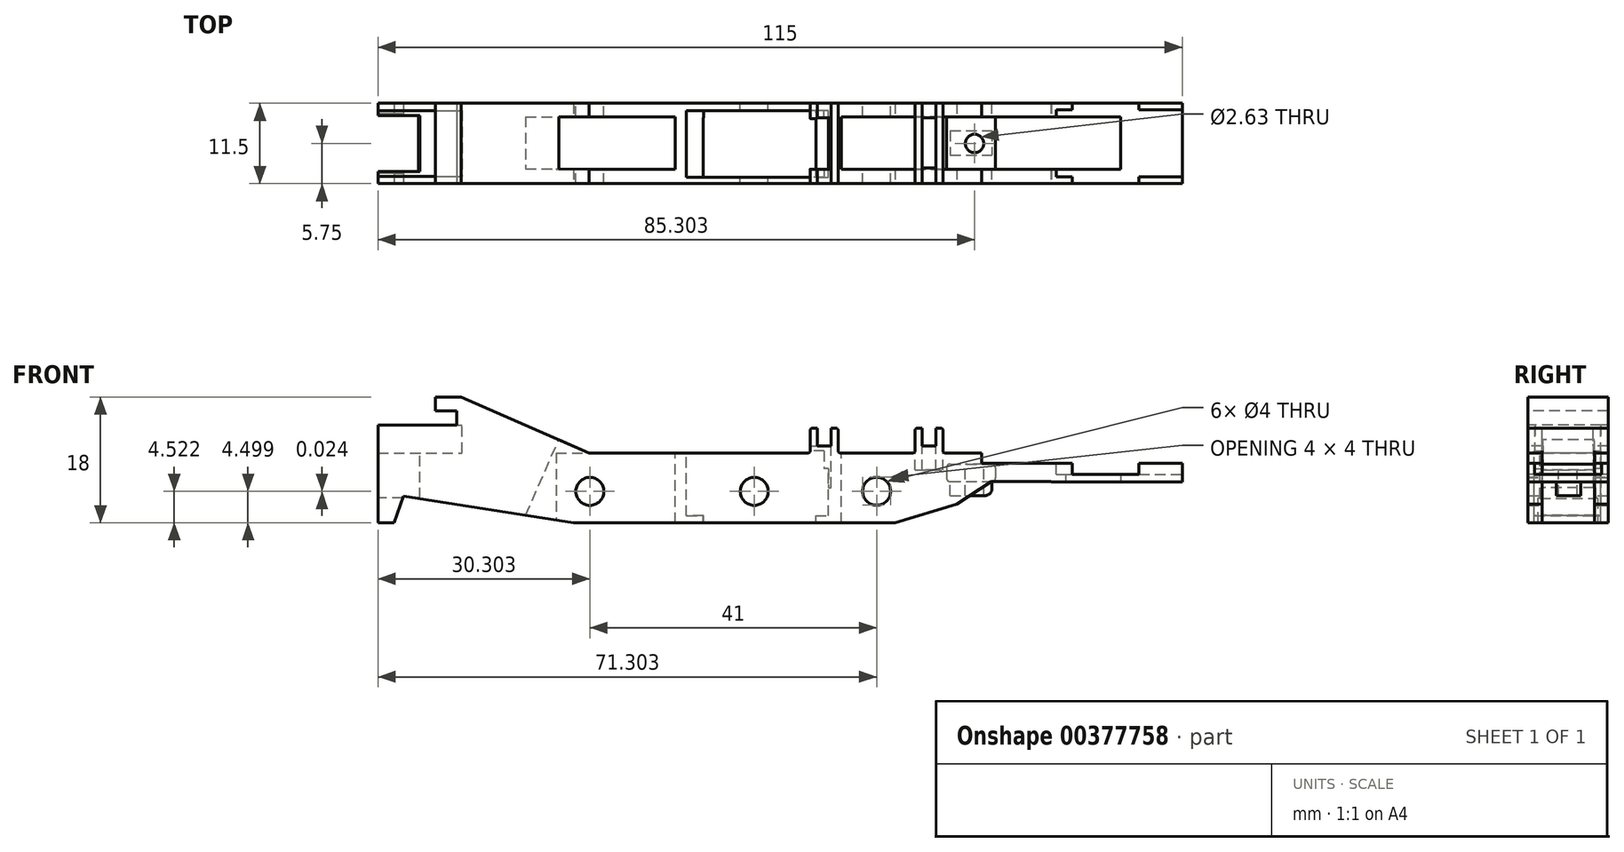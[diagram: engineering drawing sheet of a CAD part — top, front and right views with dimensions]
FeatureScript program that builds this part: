
annotation { "Feature Type Name" : "Feature", "Feature Type Description" : "" }
export const myFeature = defineFeature(function(context is Context, id is Id, definition is map)
    precondition{}
    {
        {
            var Q0;
            Q0=qCreatedBy(makeId("Front.planeOp"),FACE);
            var sketch = newSketch(context, id + "F0", { "sketchPlane" : qUnion([Q0])});
            skLineSegment(sketch, "E0.bottom", {"start": v(-37, -2.67) * mm, "end": v(77, -2.67) * mm});
            skLineSegment(sketch, "E0.top", {"start": v(-37, 7.33) * mm, "end": v(77, 7.33) * mm});
            skLineSegment(sketch, "E0.left", {"start": v(-37, -2.67) * mm, "end": v(-37, 7.33) * mm});
            skLineSegment(sketch, "E0.right", {"start": v(77, -2.67) * mm, "end": v(77, 7.33) * mm});
            skCircle(sketch, "E1", {"center": v(-7.7, 1.83) * mm, "radius": 2 * mm});
            skCircle(sketch, "E2", {"center": v(33.3, 1.85) * mm, "radius": 2 * mm});
            skCircle(sketch, "E3", {"center": v(15.8, 1.83) * mm, "radius": 2 * mm});
            skSolve(sketch);
        }
        {
            var Q0;
            Q0=makeQuery(id+"F0.imprint","IMPRINT",FACE,{"disambiguationData":[TD([[makeQuery(id+"F0.imprint","IMPRINT",EDGE,{"derivedFrom":sQuery(id+"F0.wireOp",EDGE,"E0.bottom")}),1.0]])]});
            extrude(context, id + "F1", {"entities" : qUnion([Q0]), "endBound" : BoundingType.SYMMETRIC, "depth" : 11.5 * mm});
        }
        {
            var Q0;
            Q0=makeQuery(id+"F1.opExtrude","SWEPT_FACE",FACE,{"disambiguationData":[OSD([sQuery(id+"F0.wireOp",EDGE,"E0.top")])]});
            var sketch = newSketch(context, id + "F2", { "sketchPlane" : qUnion([Q0])});
            skLineSegment(sketch, "E4.bottom", {"start": v(-33.33, 3.81) * mm, "end": v(4.47, 3.81) * mm});
            skLineSegment(sketch, "E4.top", {"start": v(-33.33, -3.69) * mm, "end": v(4.47, -3.69) * mm});
            skLineSegment(sketch, "E4.left", {"start": v(-33.33, 3.81) * mm, "end": v(-33.33, -3.69) * mm});
            skLineSegment(sketch, "E4.right", {"start": v(4.47, 3.81) * mm, "end": v(4.47, -3.69) * mm});
            skLineSegment(sketch, "E5.bottom", {"start": v(38.75, 3.81) * mm, "end": v(73.03, 3.81) * mm});
            skLineSegment(sketch, "E5.top", {"start": v(38.75, -3.69) * mm, "end": v(73.03, -3.69) * mm});
            skLineSegment(sketch, "E5.left", {"start": v(38.75, 3.81) * mm, "end": v(38.75, -3.69) * mm});
            skLineSegment(sketch, "E5.right", {"start": v(73.03, 3.81) * mm, "end": v(73.03, -3.69) * mm});
            skSolve(sketch);
        }
        {
            var Q0;
            Q0=makeQuery(id+"F2.imprint","IMPRINT",FACE,{"disambiguationData":[TD([[makeQuery(id+"F2.imprint","IMPRINT",EDGE,{"derivedFrom":sQuery(id+"F2.wireOp",EDGE,"E4.bottom")}),-1.0]])]});
            var Q1;
            Q1=makeQuery(id+"F2.imprint","IMPRINT",FACE,{"disambiguationData":[TD([[makeQuery(id+"F2.imprint","IMPRINT",EDGE,{"derivedFrom":sQuery(id+"F2.wireOp",EDGE,"E5.bottom")}),-1.0]])]});
            extrude(context, id + "F3", {"entities" : qUnion([Q0, Q1]), "operationType" : NewBodyOperationType.REMOVE, "endBound" : BoundingType.THROUGH_ALL, "oppositeDirection" : true, "depth" : 25 * mm});
        }
        {
            var Q0;
            Q0=makeQuery(id+"F1.opExtrude","SWEPT_FACE",FACE,{"disambiguationData":[OSD([sQuery(id+"F0.wireOp",EDGE,"E0.top")])]});
            var sketch = newSketch(context, id + "F4", { "sketchPlane" : qUnion([Q0])});
            skLineSegment(sketch, "E6.bottom", {"start": v(38.75, 3.81) * mm, "end": v(28.24, 3.81) * mm});
            skLineSegment(sketch, "E6.top", {"start": v(38.75, -3.69) * mm, "end": v(28.24, -3.69) * mm});
            skLineSegment(sketch, "E6.left", {"start": v(38.75, 3.81) * mm, "end": v(38.75, -3.69) * mm});
            skLineSegment(sketch, "E6.right", {"start": v(28.24, 3.81) * mm, "end": v(28.24, -3.69) * mm});
            skSolve(sketch);
        }
        {
            var Q0;
            Q0=makeQuery(id+"F4.imprint","IMPRINT",FACE,{"disambiguationData":[TD([[makeQuery(id+"F4.imprint","IMPRINT",EDGE,{"derivedFrom":sQuery(id+"F4.wireOp",EDGE,"E6.bottom")}),1.0]])]});
            extrude(context, id + "F5", {"entities" : qUnion([Q0]), "operationType" : NewBodyOperationType.REMOVE, "endBound" : BoundingType.THROUGH_ALL, "oppositeDirection" : true, "depth" : 25 * mm});
        }
        {
            var Q0;
            Q0=makeQuery(id+"F1.opExtrude","SWEPT_FACE",FACE,{"disambiguationData":[OSD([sQuery(id+"F0.wireOp",EDGE,"E0.top")])]});
            var sketch = newSketch(context, id + "F6", { "sketchPlane" : qUnion([Q0])});
            skLineSegment(sketch, "E7", {"start": v(6.12, 4.69) * mm, "end": v(6.12, -4.81) * mm});
            skLineSegment(sketch, "E8", {"start": v(6.12, -4.81) * mm, "end": v(26.4, -4.81) * mm});
            skLineSegment(sketch, "E9", {"start": v(26.4, -4.81) * mm, "end": v(26.4, 4.69) * mm});
            skLineSegment(sketch, "E10", {"start": v(26.4, 4.69) * mm, "end": v(6.12, 4.69) * mm});
            skSolve(sketch);
        }
        {
            var Q0;
            Q0=makeQuery(id+"F6.imprint","IMPRINT",FACE,{"disambiguationData":[TD([[makeQuery(id+"F6.imprint","IMPRINT",EDGE,{"derivedFrom":sQuery(id+"F6.wireOp",EDGE,"E7")}),1.0]])]});
            extrude(context, id + "F7", {"entities" : qUnion([Q0]), "operationType" : NewBodyOperationType.REMOVE, "endBound" : BoundingType.THROUGH_ALL, "oppositeDirection" : true, "depth" : 25 * mm});
        }
        {
            var Q0;
            Q0=makeQuery(id+"F1.opExtrude","CAP_FACE",FACE,{"disambiguationData":[OSD([sQuery(id+"F0.wireOp",EDGE,"E0.bottom"),sQuery(id+"F0.wireOp",EDGE,"E0.top"),sQuery(id+"F0.wireOp",EDGE,"E0.left"),sQuery(id+"F0.wireOp",EDGE,"E0.right"),sQuery(id+"F0.wireOp",EDGE,"E1"),sQuery(id+"F0.wireOp",EDGE,"saFeJPni-Uy6Z-6q54-hsxs-ZEZ7Dlqlj6Tq"),sQuery(id+"F0.wireOp",EDGE,"E2")])],"isStart":false});
            var sketch = newSketch(context, id + "F8", { "sketchPlane" : qUnion([Q0])});
            skLineSegment(sketch, "E11.bottom", {"start": v(60.3, 7.33) * mm, "end": v(75.3, 7.33) * mm});
            skLineSegment(sketch, "E11.top", {"start": v(60.3, -2.67) * mm, "end": v(75.3, -2.67) * mm});
            skLineSegment(sketch, "E11.left", {"start": v(60.3, 7.33) * mm, "end": v(60.3, -2.67) * mm});
            skLineSegment(sketch, "E11.right", {"start": v(75.3, 7.33) * mm, "end": v(75.3, -2.67) * mm});
            skSolve(sketch);
        }
        {
            var Q0;
            Q0=makeQuery(id+"F8.imprint","IMPRINT",FACE,{"disambiguationData":[TD([[makeQuery(id+"F8.imprint","IMPRINT",EDGE,{"derivedFrom":sQuery(id+"F8.wireOp",EDGE,"E11.bottom")}),-1.0]])]});
            extrude(context, id + "F9", {"entities" : qUnion([Q0]), "operationType" : NewBodyOperationType.ADD, "oppositeDirection" : true, "depth" : 11.5 * mm});
        }
        {
            var Q0;
            Q0=makeQuery(id+"F9.boolean.opBoolean","MERGE",FACE,{"derivedFrom":[makeQuery(id+"F1.opExtrude","SWEPT_FACE",FACE,{"disambiguationData":[OSD([sQuery(id+"F0.wireOp",EDGE,"E0.top")])]}),makeQuery(id+"F9.opExtrude","SWEPT_FACE",FACE,{"disambiguationData":[OSD([sQuery(id+"F8.wireOp",EDGE,"E11.bottom")])]})]});
            var sketch = newSketch(context, id + "F10", { "sketchPlane" : qUnion([Q0])});
            skArc(sketch, "E12", {"start": v(65.32, 1) * mm, "mid": v(64.3, -0.01) * mm, "end": v(65.34, -1) * mm});
            skArc(sketch, "E13", {"start": v(66.8, -1) * mm, "mid": v(67.8, 0) * mm, "end": v(66.8, 1) * mm});
            skLineSegment(sketch, "E14", {"start": v(65.28, 1) * mm, "end": v(66.8, 1) * mm});
            skLineSegment(sketch, "E15", {"start": v(65.34, -1) * mm, "end": v(66.8, -1) * mm});
            skSolve(sketch);
        }
        {
            var Q0;
            {var subQ3=sQuery(id+"F10.wireOp",EDGE,"E12");Q0=makeQuery(id+"F10.imprint","IMPRINT",FACE,{"disambiguationData":[TD([[makeQuery(id+"F10.imprint","IMPRINT",EDGE,{"derivedFrom":subQ3}),1.0]])]});}
            extrude(context, id + "F11", {"entities" : qUnion([Q0]), "operationType" : NewBodyOperationType.REMOVE, "endBound" : BoundingType.THROUGH_ALL, "oppositeDirection" : true, "depth" : 25 * mm});
        }
        {
            var Q0;
            Q0=makeQuery(id+"F1.opExtrude","CAP_FACE",FACE,{"disambiguationData":[OSD([sQuery(id+"F0.wireOp",EDGE,"E0.bottom"),sQuery(id+"F0.wireOp",EDGE,"E0.top"),sQuery(id+"F0.wireOp",EDGE,"E0.left"),sQuery(id+"F0.wireOp",EDGE,"E0.right"),sQuery(id+"F0.wireOp",EDGE,"E1"),sQuery(id+"F0.wireOp",EDGE,"saFeJPni-Uy6Z-6q54-hsxs-ZEZ7Dlqlj6Tq"),sQuery(id+"F0.wireOp",EDGE,"E2")])],"isStart":false});
            var sketch = newSketch(context, id + "F12", { "sketchPlane" : qUnion([Q0])});
            skLineSegment(sketch, "E16.bottom", {"start": v(48.3, 7.33) * mm, "end": v(77, 7.33) * mm});
            skLineSegment(sketch, "E16.top", {"start": v(48.3, 5.83) * mm, "end": v(61.3, 5.83) * mm});
            skLineSegment(sketch, "E16.left", {"start": v(48.3, 7.33) * mm, "end": v(48.3, 5.83) * mm});
            skLineSegment(sketch, "E16.right", {"start": v(77, 7.33) * mm, "end": v(77, 5.83) * mm});
            skLineSegment(sketch, "E17.top", {"start": v(61.3, 4.23) * mm, "end": v(70.8, 4.23) * mm});
            skLineSegment(sketch, "E17.left", {"start": v(61.3, 5.83) * mm, "end": v(61.3, 4.23) * mm});
            skLineSegment(sketch, "E17.right", {"start": v(70.8, 5.83) * mm, "end": v(70.8, 4.23) * mm});
            skLineSegment(sketch, "E18.trimOffspring", {"start": v(70.8, 5.83) * mm, "end": v(77, 5.83) * mm});
            skSolve(sketch);
        }
        {
            var Q0;
            Q0=makeQuery(id+"F12.imprint","IMPRINT",FACE,{"disambiguationData":[TD([[makeQuery(id+"F12.imprint","IMPRINT",EDGE,{"derivedFrom":sQuery(id+"F12.wireOp",EDGE,"E16.bottom")}),-1.0]])]});
            extrude(context, id + "F13", {"entities" : qUnion([Q0]), "operationType" : NewBodyOperationType.REMOVE, "endBound" : BoundingType.THROUGH_ALL, "oppositeDirection" : true, "depth" : 25 * mm});
        }
        {
            var Q0;
            Q0=makeQuery(id+"F1.opExtrude","CAP_FACE",FACE,{"disambiguationData":[OSD([sQuery(id+"F0.wireOp",EDGE,"E0.bottom"),sQuery(id+"F0.wireOp",EDGE,"E0.top"),sQuery(id+"F0.wireOp",EDGE,"E0.left"),sQuery(id+"F0.wireOp",EDGE,"E0.right"),sQuery(id+"F0.wireOp",EDGE,"E1"),sQuery(id+"F0.wireOp",EDGE,"saFeJPni-Uy6Z-6q54-hsxs-ZEZ7Dlqlj6Tq"),sQuery(id+"F0.wireOp",EDGE,"E2")])],"isStart":false});
            var sketch = newSketch(context, id + "F14", { "sketchPlane" : qUnion([Q0])});
            skLineSegment(sketch, "E19.bottom", {"start": v(50, -2.67) * mm, "end": v(77, -2.67) * mm});
            skLineSegment(sketch, "E19.top", {"start": v(50, 1.58) * mm, "end": v(77, 1.58) * mm});
            skLineSegment(sketch, "E19.right", {"start": v(77, -2.67) * mm, "end": v(77, 1.58) * mm});
            skLineSegment(sketch, "E20", {"start": v(50, 1.58) * mm, "end": v(35.95, -2.67) * mm});
            skSolve(sketch);
        }
        {
            var Q0;
            {var subQ1=sQuery(id+"F14.wireOp",EDGE,"E19.bottom");Q0=makeQuery(id+"F14.imprint","IMPRINT",FACE,{"disambiguationData":[TD([[makeQuery(id+"F14.imprint","IMPRINT",EDGE,{"derivedFrom":subQ1}),1.0]])]});}
            extrude(context, id + "F15", {"entities" : qUnion([Q0]), "operationType" : NewBodyOperationType.REMOVE, "endBound" : BoundingType.THROUGH_ALL, "oppositeDirection" : true, "depth" : 25 * mm});
        }
        {
            var Q0;
            Q0=makeQuery(id+"F1.opExtrude","CAP_FACE",FACE,{"disambiguationData":[OSD([sQuery(id+"F0.wireOp",EDGE,"E0.bottom"),sQuery(id+"F0.wireOp",EDGE,"E0.top"),sQuery(id+"F0.wireOp",EDGE,"E0.left"),sQuery(id+"F0.wireOp",EDGE,"E0.right"),sQuery(id+"F0.wireOp",EDGE,"E1"),sQuery(id+"F0.wireOp",EDGE,"saFeJPni-Uy6Z-6q54-hsxs-ZEZ7Dlqlj6Tq"),sQuery(id+"F0.wireOp",EDGE,"E2")])],"isStart":false});
            var sketch = newSketch(context, id + "F16", { "sketchPlane" : qUnion([Q0])});
            skLineSegment(sketch, "E21.bottom", {"start": v(-37, 7.33) * mm, "end": v(-12.53, 7.33) * mm});
            skLineSegment(sketch, "E21.top", {"start": v(-37, -2.67) * mm, "end": v(-12.53, -2.67) * mm});
            skLineSegment(sketch, "E21.left", {"start": v(-37, 7.33) * mm, "end": v(-37, -2.67) * mm});
            skLineSegment(sketch, "E21.right", {"start": v(-12.53, 7.33) * mm, "end": v(-12.53, -2.67) * mm});
            skSolve(sketch);
        }
        {
            var Q0;
            Q0=makeQuery(id+"F16.imprint","IMPRINT",FACE,{"disambiguationData":[TD([[makeQuery(id+"F16.imprint","IMPRINT",EDGE,{"derivedFrom":sQuery(id+"F16.wireOp",EDGE,"E21.bottom")}),-1.0]])]});
            extrude(context, id + "F17", {"entities" : qUnion([Q0]), "operationType" : NewBodyOperationType.ADD, "oppositeDirection" : true, "depth" : 11.5 * mm});
        }
        {
            var Q0;
            Q0=makeQuery(id+"F1.opExtrude","CAP_FACE",FACE,{"disambiguationData":[OSD([sQuery(id+"F0.wireOp",EDGE,"E0.bottom"),sQuery(id+"F0.wireOp",EDGE,"E0.top"),sQuery(id+"F0.wireOp",EDGE,"E0.left"),sQuery(id+"F0.wireOp",EDGE,"E0.right"),sQuery(id+"F0.wireOp",EDGE,"E1"),sQuery(id+"F0.wireOp",EDGE,"saFeJPni-Uy6Z-6q54-hsxs-ZEZ7Dlqlj6Tq"),sQuery(id+"F0.wireOp",EDGE,"E2")])],"isStart":false});
            var sketch = newSketch(context, id + "F18", { "sketchPlane" : qUnion([Q0])});
            skLineSegment(sketch, "E22", {"start": v(-37, -2.67) * mm, "end": v(-37, 1.59) * mm});
            skLineSegment(sketch, "E23", {"start": v(-37, 1.59) * mm, "end": v(-10.02, -2.67) * mm});
            skLineSegment(sketch, "E24", {"start": v(-10.02, -2.67) * mm, "end": v(-37, -2.67) * mm});
            skSolve(sketch);
        }
        {
            var Q0;
            Q0=makeQuery(id+"F18.imprint","IMPRINT",FACE,{"disambiguationData":[TD([[makeQuery(id+"F18.imprint","IMPRINT",EDGE,{"derivedFrom":sQuery(id+"F18.wireOp",EDGE,"E22")}),-1.0]])]});
            extrude(context, id + "F19", {"entities" : qUnion([Q0]), "operationType" : NewBodyOperationType.REMOVE, "oppositeDirection" : true, "depth" : 11.5 * mm});
        }
        {
            var Q0;
            Q0=makeQuery(id+"F1.opExtrude","CAP_FACE",FACE,{"disambiguationData":[OSD([sQuery(id+"F0.wireOp",EDGE,"E0.bottom"),sQuery(id+"F0.wireOp",EDGE,"E0.top"),sQuery(id+"F0.wireOp",EDGE,"E0.left"),sQuery(id+"F0.wireOp",EDGE,"E0.right"),sQuery(id+"F0.wireOp",EDGE,"E1"),sQuery(id+"F0.wireOp",EDGE,"saFeJPni-Uy6Z-6q54-hsxs-ZEZ7Dlqlj6Tq"),sQuery(id+"F0.wireOp",EDGE,"E2")])],"isStart":false});
            var sketch = newSketch(context, id + "F20", { "sketchPlane" : qUnion([Q0])});
            skLineSegment(sketch, "E25", {"start": v(44.78, 0) * mm, "end": v(49.72, 3.23) * mm});
            skLineSegment(sketch, "E26", {"start": v(49.72, 3.23) * mm, "end": v(58.21, 3.23) * mm});
            skLineSegment(sketch, "E27", {"start": v(58.21, 3.23) * mm, "end": v(59.75, 1.58) * mm});
            skLineSegment(sketch, "E28", {"start": v(59.75, 1.58) * mm, "end": v(50, 1.58) * mm});
            skLineSegment(sketch, "E29", {"start": v(50, 1.58) * mm, "end": v(44.78, 0) * mm});
            skSolve(sketch);
        }
        {
            var Q0;
            Q0 = qSketchRegion(id + "F20", true);
            extrude(context, id + "F21", {"entities" : qUnion([Q0]), "operationType" : NewBodyOperationType.REMOVE, "oppositeDirection" : true, "depth" : 11.5 * mm});
        }
        {
            var Q0;
            Q0=makeQuery(id+"F1.opExtrude","CAP_FACE",FACE,{"disambiguationData":[OSD([sQuery(id+"F0.wireOp",EDGE,"E0.bottom"),sQuery(id+"F0.wireOp",EDGE,"E0.top"),sQuery(id+"F0.wireOp",EDGE,"E0.left"),sQuery(id+"F0.wireOp",EDGE,"E0.right"),sQuery(id+"F0.wireOp",EDGE,"E1"),sQuery(id+"F0.wireOp",EDGE,"saFeJPni-Uy6Z-6q54-hsxs-ZEZ7Dlqlj6Tq"),sQuery(id+"F0.wireOp",EDGE,"E2")])],"isStart":false});
            var sketch = newSketch(context, id + "F22", { "sketchPlane" : qUnion([Q0])});
            skLineSegment(sketch, "E30.bottom", {"start": v(43.3, 5.73) * mm, "end": v(50.3, 5.73) * mm});
            skLineSegment(sketch, "E30.top", {"start": v(43.3, 3.23) * mm, "end": v(50.3, 3.23) * mm});
            skLineSegment(sketch, "E30.left", {"start": v(43.3, 5.73) * mm, "end": v(43.3, 3.23) * mm});
            skLineSegment(sketch, "E30.right", {"start": v(50.3, 5.73) * mm, "end": v(50.3, 3.23) * mm});
            skSolve(sketch);
        }
        {
            var Q0;
            Q0=makeQuery(id+"F22.imprint","IMPRINT",FACE,{"disambiguationData":[TD([[makeQuery(id+"F22.imprint","IMPRINT",EDGE,{"derivedFrom":sQuery(id+"F22.wireOp",EDGE,"E30.bottom")}),-1.0]])]});
            extrude(context, id + "F23", {"entities" : qUnion([Q0]), "operationType" : NewBodyOperationType.ADD, "oppositeDirection" : true, "depth" : 11.5 * mm});
        }
        {
            var Q0;
            Q0=makeQuery(id+"F23.opExtrude","SWEPT_EDGE",EDGE,{"disambiguationData":[OSD([sQuery(id+"F22.wireOp",EDGE,"E30.bottom"),sQuery(id+"F22.wireOp",EDGE,"E30.left")])]});
            var Q1;
            Q1=makeQuery(id+"F23.opExtrude","SWEPT_EDGE",EDGE,{"disambiguationData":[OSD([sQuery(id+"F22.wireOp",EDGE,"E30.bottom"),sQuery(id+"F22.wireOp",EDGE,"E30.right")])]});
            var Q2;
            Q2=makeQuery(id+"F23.opExtrude","SWEPT_EDGE",EDGE,{"disambiguationData":[OSD([sQuery(id+"F20.wireOp",EDGE,"E26"),sQuery(id+"F22.wireOp",EDGE,"E30.top"),sQuery(id+"F22.wireOp",EDGE,"E30.right")])]});
            var Q3;
            Q3=makeQuery(id+"F23.opExtrude","SWEPT_EDGE",EDGE,{"disambiguationData":[OSD([sQuery(id+"F22.wireOp",EDGE,"E30.top"),sQuery(id+"F22.wireOp",EDGE,"E30.left")])]});
            fillet(context, id + "F24", {"entities" : qUnion([Q0, Q1, Q2, Q3]), "radius" : 0.5 * mm, "tangentPropagation" : true, "allowEdgeOverflow" : false});
        }
        {
            var Q0;
            Q0=makeQuery(id+"F23.opExtrude","SWEPT_FACE",FACE,{"disambiguationData":[OSD([sQuery(id+"F22.wireOp",EDGE,"E30.bottom")])]});
            var sketch = newSketch(context, id + "F25", { "sketchPlane" : qUnion([Q0])});
            skCircle(sketch, "E31", {"center": v(47.3, 0) * mm, "radius": 1.31 * mm});
            skSolve(sketch);
        }
        {
            var Q0;
            Q0=makeQuery(id+"F25.imprint","IMPRINT",FACE,{"disambiguationData":[TD([[makeQuery(id+"F25.imprint","IMPRINT",EDGE,{"derivedFrom":sQuery(id+"F25.wireOp",EDGE,"E31")}),1.0]])]});
            var Q1;
            Q1=sQuery(id+"F25.wireOp",EDGE,"E31");
            extrude(context, id + "F26", {"entities" : qUnion([Q0]), "operationType" : NewBodyOperationType.REMOVE, "surfaceEntities" : qUnion([Q1]), "endBound" : BoundingType.UP_TO_NEXT, "oppositeDirection" : true, "depth" : 25 * mm});
        }
        {
            var Q0;
            Q0=makeQuery(id+"F1.opExtrude","CAP_FACE",FACE,{"disambiguationData":[OSD([sQuery(id+"F0.wireOp",EDGE,"E0.bottom"),sQuery(id+"F0.wireOp",EDGE,"E0.top"),sQuery(id+"F0.wireOp",EDGE,"E0.left"),sQuery(id+"F0.wireOp",EDGE,"E0.right"),sQuery(id+"F0.wireOp",EDGE,"E1"),sQuery(id+"F0.wireOp",EDGE,"saFeJPni-Uy6Z-6q54-hsxs-ZEZ7Dlqlj6Tq"),sQuery(id+"F0.wireOp",EDGE,"E2")])],"isStart":false});
            var sketch = newSketch(context, id + "F27", { "sketchPlane" : qUnion([Q0])});
            skLineSegment(sketch, "E32", {"start": v(-7.82, 7.33) * mm, "end": v(-23.82, 14.33) * mm});
            skLineSegment(sketch, "E33", {"start": v(-23.82, 7.33) * mm, "end": v(-7.82, 7.33) * mm});
            skLineSegment(sketch, "E34", {"start": v(-23.82, 14.33) * mm, "end": v(-28.8, 14.33) * mm});
            skLineSegment(sketch, "E35", {"start": v(-28.8, 14.33) * mm, "end": v(-28.8, 12.33) * mm});
            skLineSegment(sketch, "E36", {"start": v(-28.8, 12.33) * mm, "end": v(-24.75, 12.33) * mm});
            skLineSegment(sketch, "E37", {"start": v(-24.75, 12.33) * mm, "end": v(-24.75, 9.33) * mm});
            skLineSegment(sketch, "E38", {"start": v(-24.75, 9.33) * mm, "end": v(-28.8, 9.33) * mm});
            skLineSegment(sketch, "E39", {"start": v(-28.8, 9.33) * mm, "end": v(-37, 9.33) * mm});
            skLineSegment(sketch, "E40", {"start": v(-37, 9.33) * mm, "end": v(-37, 7.33) * mm});
            skSolve(sketch);
        }
        {
            var Q0;
            Q0=makeQuery(id+"F27.imprint","IMPRINT",FACE,{"disambiguationData":[TD([[makeQuery(id+"F27.imprint","IMPRINT",EDGE,{"derivedFrom":sQuery(id+"F27.wireOp",EDGE,"E32")}),1.0]])]});
            extrude(context, id + "F28", {"entities" : qUnion([Q0]), "operationType" : NewBodyOperationType.ADD, "oppositeDirection" : true, "depth" : 11.5 * mm});
        }
        {
            var Q0;
            Q0=makeQuery(id+"F28.opExtrude","SWEPT_FACE",FACE,{"disambiguationData":[OSD([sQuery(id+"F27.wireOp",EDGE,"E32")])]});
            var sketch = newSketch(context, id + "F29", { "sketchPlane" : qUnion([Q0])});
            skLineSegment(sketch, "E41", {"start": v(-10.1, 3.81) * mm, "end": v(-14.83, 3.81) * mm});
            skLineSegment(sketch, "E42", {"start": v(-14.83, 3.81) * mm, "end": v(-14.83, -3.65) * mm});
            skLineSegment(sketch, "E43", {"start": v(-14.83, -3.65) * mm, "end": v(-10.1, -3.69) * mm});
            skSolve(sketch);
        }
        {
            var Q0;
            Q0=makeQuery(id+"F29.imprint","IMPRINT",FACE,{"disambiguationData":[TD([[makeQuery(id+"F29.imprint","IMPRINT",EDGE,{"derivedFrom":sQuery(id+"F29.wireOp",EDGE,"E41")}),1.0]])]});
            extrude(context, id + "F30", {"entities" : qUnion([Q0]), "operationType" : NewBodyOperationType.REMOVE, "endBound" : BoundingType.UP_TO_NEXT, "oppositeDirection" : true, "depth" : 25 * mm});
        }
        {
            var Q0;
            {var subQ0=sQuery(id+"F0.wireOp",EDGE,"E0.top");Q0=makeQuery(id+"F28.boolean.opBoolean","MERGE",FACE,{"derivedFrom":[makeQuery(id+"F1.opExtrude","CAP_FACE",FACE,{"disambiguationData":[OSD([sQuery(id+"F0.wireOp",EDGE,"E0.bottom"),subQ0,sQuery(id+"F0.wireOp",EDGE,"E0.left"),sQuery(id+"F0.wireOp",EDGE,"E0.right"),sQuery(id+"F0.wireOp",EDGE,"E1"),sQuery(id+"F0.wireOp",EDGE,"saFeJPni-Uy6Z-6q54-hsxs-ZEZ7Dlqlj6Tq"),sQuery(id+"F0.wireOp",EDGE,"E2")])],"isStart":false}),makeQuery(id+"F28.opExtrude","CAP_FACE",FACE,{"disambiguationData":[OSD([subQ0,sQuery(id+"F27.wireOp",EDGE,"E32"),sQuery(id+"F27.wireOp",EDGE,"E33"),sQuery(id+"F27.wireOp",EDGE,"E34"),sQuery(id+"F27.wireOp",EDGE,"E35"),sQuery(id+"F27.wireOp",EDGE,"E36"),sQuery(id+"F27.wireOp",EDGE,"E37"),sQuery(id+"F27.wireOp",EDGE,"E38"),sQuery(id+"F27.wireOp",EDGE,"E39"),sQuery(id+"F27.wireOp",EDGE,"E40")])],"isStart":true})]});}
            var sketch = newSketch(context, id + "F31", { "sketchPlane" : qUnion([Q0])});
            skLineSegment(sketch, "E44", {"start": v(-37, 1.59) * mm, "end": v(-37, -2.63) * mm});
            skLineSegment(sketch, "E45", {"start": v(-37, -2.63) * mm, "end": v(-35.69, -2.63) * mm});
            skLineSegment(sketch, "E46", {"start": v(-35.69, -2.63) * mm, "end": v(-34.34, 1.17) * mm});
            skSolve(sketch);
        }
        {
            var Q0;
            {var subQ0=sQuery(id+"F31.wireOp",EDGE,"E44");Q0=makeQuery(id+"F31.imprint","IMPRINT",FACE,{"disambiguationData":[TD([[makeQuery(id+"F31.imprint","IMPRINT",EDGE,{"derivedFrom":subQ0}),1.0]])]});}
            extrude(context, id + "F32", {"entities" : qUnion([Q0]), "operationType" : NewBodyOperationType.ADD, "oppositeDirection" : true, "depth" : 11.5 * mm});
        }
        {
            var Q0;
            Q0=makeQuery(id+"F32.boolean.opBoolean","MERGE",FACE,{"derivedFrom":[makeQuery(id+"F1.opExtrude","SWEPT_FACE",FACE,{"disambiguationData":[OSD([sQuery(id+"F0.wireOp",EDGE,"E0.left")])]}),makeQuery(id+"F32.opExtrude","SWEPT_FACE",FACE,{"disambiguationData":[OSD([sQuery(id+"F31.wireOp",EDGE,"E44")])]})]});
            var sketch = newSketch(context, id + "F33", { "sketchPlane" : qUnion([Q0])});
            skLineSegment(sketch, "E47", {"start": v(-4.25, -2.63) * mm, "end": v(-4.25, 0.87) * mm});
            skLineSegment(sketch, "E48", {"start": v(-4.25, 0.87) * mm, "end": v(4.25, 0.87) * mm});
            skLineSegment(sketch, "E49", {"start": v(4.25, 0.87) * mm, "end": v(4.25, -2.63) * mm});
            skSolve(sketch);
        }
        {
            var Q0;
            {var subQ0=sQuery(id+"F33.wireOp",EDGE,"E47");Q0=makeQuery(id+"F33.imprint","IMPRINT",FACE,{"disambiguationData":[TD([[makeQuery(id+"F33.imprint","IMPRINT",EDGE,{"derivedFrom":subQ0}),-1.0]])]});}
            extrude(context, id + "F34", {"entities" : qUnion([Q0]), "operationType" : NewBodyOperationType.REMOVE, "oppositeDirection" : true, "depth" : 3 * mm});
        }
        {
            var Q0;
            {var subQ9=makeQuery(id+"F21.opExtrude","SWEPT_FACE",FACE,{"disambiguationData":[OSD([sQuery(id+"F20.wireOp",EDGE,"E26")])]});Q0=makeQuery(id+"F24.opFillet","SPLIT",FACE,{"disambiguationData":[OD(2.0)],"derivedFrom":makeQuery(id+"F23.boolean.opBoolean","MERGE",FACE,{"derivedFrom":[makeQuery(id+"F21.boolean.opBoolean","COPY",FACE,{"disambiguationData":[TD([makeQuery(id+"F3.boolean.opBoolean","COPY",FACE,{"derivedFrom":makeQuery(id+"F3.opExtrude","SWEPT_FACE",FACE,{"disambiguationData":[OSD([sQuery(id+"F2.wireOp",EDGE,"E5.top")])]})})])],"derivedFrom":subQ9}),makeQuery(id+"F21.boolean.opBoolean","COPY",FACE,{"disambiguationData":[TD([makeQuery(id+"F3.boolean.opBoolean","COPY",FACE,{"derivedFrom":makeQuery(id+"F3.opExtrude","SWEPT_FACE",FACE,{"disambiguationData":[OSD([sQuery(id+"F2.wireOp",EDGE,"E5.bottom")])]})})])],"derivedFrom":subQ9}),makeQuery(id+"F23.opExtrude","SWEPT_FACE",FACE,{"disambiguationData":[OSD([sQuery(id+"F22.wireOp",EDGE,"E30.top")])]})]})});}
            var sketch = newSketch(context, id + "F35", { "sketchPlane" : qUnion([Q0])});
            skLineSegment(sketch, "E50.bottom", {"start": v(43.8, 1.69) * mm, "end": v(49.8, 1.69) * mm});
            skLineSegment(sketch, "E50.top", {"start": v(43.8, -1.81) * mm, "end": v(49.8, -1.81) * mm});
            skLineSegment(sketch, "E50.left", {"start": v(43.8, 1.69) * mm, "end": v(43.8, -1.81) * mm});
            skLineSegment(sketch, "E50.right", {"start": v(49.8, 1.69) * mm, "end": v(49.8, -1.81) * mm});
            skSolve(sketch);
        }
        {
            var Q0;
            Q0=makeQuery(id+"F35.imprint","IMPRINT",FACE,{"disambiguationData":[TD([[makeQuery(id+"F35.imprint","IMPRINT",EDGE,{"derivedFrom":sQuery(id+"F35.wireOp",EDGE,"E50.bottom")}),-1.0]])]});
            extrude(context, id + "F36", {"entities" : qUnion([Q0]), "operationType" : NewBodyOperationType.ADD, "depth" : 2 * mm});
        }
        {
            var Q0;
            Q0=makeQuery(id+"F36.opExtrude","CAP_EDGE",EDGE,{"disambiguationData":[OSD([sQuery(id+"F35.wireOp",EDGE,"E50.right")])],"isStart":false});
            fillet(context, id + "F37", {"entities" : qUnion([Q0]), "radius" : 1 * mm, "tangentPropagation" : true, "allowEdgeOverflow" : false});
        }
        {
            var Q0;
            {var subQ0=sQuery(id+"F0.wireOp",EDGE,"E0.top");Q0=makeQuery(id+"F32.boolean.opBoolean","MERGE",FACE,{"derivedFrom":[makeQuery(id+"F28.boolean.opBoolean","MERGE",FACE,{"derivedFrom":[makeQuery(id+"F1.opExtrude","CAP_FACE",FACE,{"disambiguationData":[OSD([sQuery(id+"F0.wireOp",EDGE,"E0.bottom"),subQ0,sQuery(id+"F0.wireOp",EDGE,"E0.left"),sQuery(id+"F0.wireOp",EDGE,"E0.right"),sQuery(id+"F0.wireOp",EDGE,"E1"),sQuery(id+"F0.wireOp",EDGE,"saFeJPni-Uy6Z-6q54-hsxs-ZEZ7Dlqlj6Tq"),sQuery(id+"F0.wireOp",EDGE,"E2")])],"isStart":false}),makeQuery(id+"F28.opExtrude","CAP_FACE",FACE,{"disambiguationData":[OSD([subQ0,sQuery(id+"F27.wireOp",EDGE,"E32"),sQuery(id+"F27.wireOp",EDGE,"E33"),sQuery(id+"F27.wireOp",EDGE,"E34"),sQuery(id+"F27.wireOp",EDGE,"E35"),sQuery(id+"F27.wireOp",EDGE,"E36"),sQuery(id+"F27.wireOp",EDGE,"E37"),sQuery(id+"F27.wireOp",EDGE,"E38"),sQuery(id+"F27.wireOp",EDGE,"E39"),sQuery(id+"F27.wireOp",EDGE,"E40")])],"isStart":true})]}),makeQuery(id+"F32.opExtrude","CAP_FACE",FACE,{"disambiguationData":[OSD([sQuery(id+"F18.wireOp",EDGE,"E23"),sQuery(id+"F31.wireOp",EDGE,"E44"),sQuery(id+"F31.wireOp",EDGE,"E45"),sQuery(id+"F31.wireOp",EDGE,"E46")])],"isStart":true})]});}
            var sketch = newSketch(context, id + "F38", { "sketchPlane" : qUnion([Q0])});
            skLineSegment(sketch, "E51.bottom", {"start": v(5.67, -2.67) * mm, "end": v(27.36, -2.67) * mm});
            skLineSegment(sketch, "E51.top", {"start": v(5.67, -1.67) * mm, "end": v(27.36, -1.67) * mm});
            skLineSegment(sketch, "E51.left", {"start": v(5.67, -2.67) * mm, "end": v(5.67, -1.67) * mm});
            skLineSegment(sketch, "E51.right", {"start": v(27.36, -2.67) * mm, "end": v(27.36, -1.67) * mm});
            skSolve(sketch);
        }
        {
            var Q0;
            Q0=makeQuery(id+"F38.imprint","IMPRINT",FACE,{"disambiguationData":[TD([[makeQuery(id+"F38.imprint","IMPRINT",EDGE,{"derivedFrom":sQuery(id+"F38.wireOp",EDGE,"E51.bottom")}),1.0]])]});
            extrude(context, id + "F39", {"entities" : qUnion([Q0]), "operationType" : NewBodyOperationType.ADD, "oppositeDirection" : true, "depth" : 11.5 * mm});
        }
        {
            var Q0;
            Q0=makeQuery(id+"F39.opExtrude","SWEPT_FACE",FACE,{"disambiguationData":[OSD([sQuery(id+"F38.wireOp",EDGE,"E51.top")])]});
            var sketch = newSketch(context, id + "F40", { "sketchPlane" : qUnion([Q0])});
            skLineSegment(sketch, "E52.bottom", {"start": v(12.77, 3.69) * mm, "end": v(24.6, 3.69) * mm});
            skLineSegment(sketch, "E52.top", {"start": v(12.77, -3.81) * mm, "end": v(24.6, -3.81) * mm});
            skLineSegment(sketch, "E52.left", {"start": v(12.77, 3.69) * mm, "end": v(12.77, -3.81) * mm});
            skLineSegment(sketch, "E52.right", {"start": v(24.6, 3.69) * mm, "end": v(24.6, -3.81) * mm});
            skSolve(sketch);
        }
        {
            var Q0;
            Q0=makeQuery(id+"F40.imprint","IMPRINT",FACE,{"disambiguationData":[TD([[makeQuery(id+"F40.imprint","IMPRINT",EDGE,{"derivedFrom":sQuery(id+"F40.wireOp",EDGE,"E52.bottom")}),-1.0]])]});
            extrude(context, id + "F41", {"entities" : qUnion([Q0]), "operationType" : NewBodyOperationType.REMOVE, "endBound" : BoundingType.UP_TO_NEXT, "oppositeDirection" : true, "depth" : 25 * mm});
        }
        {
            var Q0;
            {var subQ0=sQuery(id+"F0.wireOp",EDGE,"E0.top");Q0=makeQuery(id+"F32.boolean.opBoolean","MERGE",FACE,{"derivedFrom":[makeQuery(id+"F28.boolean.opBoolean","MERGE",FACE,{"derivedFrom":[makeQuery(id+"F1.opExtrude","CAP_FACE",FACE,{"disambiguationData":[OSD([sQuery(id+"F0.wireOp",EDGE,"E0.bottom"),subQ0,sQuery(id+"F0.wireOp",EDGE,"E0.left"),sQuery(id+"F0.wireOp",EDGE,"E0.right"),sQuery(id+"F0.wireOp",EDGE,"E1"),sQuery(id+"F0.wireOp",EDGE,"saFeJPni-Uy6Z-6q54-hsxs-ZEZ7Dlqlj6Tq"),sQuery(id+"F0.wireOp",EDGE,"E2")])],"isStart":false}),makeQuery(id+"F28.opExtrude","CAP_FACE",FACE,{"disambiguationData":[OSD([subQ0,sQuery(id+"F27.wireOp",EDGE,"E32"),sQuery(id+"F27.wireOp",EDGE,"E33"),sQuery(id+"F27.wireOp",EDGE,"E34"),sQuery(id+"F27.wireOp",EDGE,"E35"),sQuery(id+"F27.wireOp",EDGE,"E36"),sQuery(id+"F27.wireOp",EDGE,"E37"),sQuery(id+"F27.wireOp",EDGE,"E38"),sQuery(id+"F27.wireOp",EDGE,"E39"),sQuery(id+"F27.wireOp",EDGE,"E40")])],"isStart":true})]}),makeQuery(id+"F32.opExtrude","CAP_FACE",FACE,{"disambiguationData":[OSD([sQuery(id+"F18.wireOp",EDGE,"E23"),sQuery(id+"F31.wireOp",EDGE,"E44"),sQuery(id+"F31.wireOp",EDGE,"E45"),sQuery(id+"F31.wireOp",EDGE,"E46")])],"isStart":true})]});}
            var sketch = newSketch(context, id + "F42", { "sketchPlane" : qUnion([Q0])});
            skLineSegment(sketch, "E53.bottom", {"start": v(23.8, 5.07) * mm, "end": v(27.8, 5.07) * mm});
            skLineSegment(sketch, "E53.top", {"start": v(23.8, 10.85) * mm, "end": v(24.8, 10.85) * mm});
            skLineSegment(sketch, "E53.left", {"start": v(23.8, 5.07) * mm, "end": v(23.8, 10.85) * mm});
            skLineSegment(sketch, "E53.right", {"start": v(27.8, 5.07) * mm, "end": v(27.8, 10.85) * mm});
            skLineSegment(sketch, "E54.bottom", {"start": v(38.8, 4.87) * mm, "end": v(42.8, 4.87) * mm});
            skLineSegment(sketch, "E54.top", {"start": v(38.8, 10.85) * mm, "end": v(39.8, 10.85) * mm});
            skLineSegment(sketch, "E54.left", {"start": v(38.8, 4.87) * mm, "end": v(38.8, 10.85) * mm});
            skLineSegment(sketch, "E54.right", {"start": v(42.8, 4.87) * mm, "end": v(42.8, 10.85) * mm});
            skLineSegment(sketch, "E55", {"start": v(24.8, 10.85) * mm, "end": v(24.8, 8.35) * mm});
            skLineSegment(sketch, "E56", {"start": v(24.8, 8.35) * mm, "end": v(26.8, 8.35) * mm});
            skLineSegment(sketch, "E57", {"start": v(26.8, 8.35) * mm, "end": v(26.8, 10.85) * mm});
            skLineSegment(sketch, "E58", {"start": v(39.8, 10.85) * mm, "end": v(39.8, 8.35) * mm});
            skLineSegment(sketch, "E59", {"start": v(39.8, 8.35) * mm, "end": v(41.8, 8.35) * mm});
            skLineSegment(sketch, "E60", {"start": v(41.8, 8.35) * mm, "end": v(41.8, 10.85) * mm});
            skLineSegment(sketch, "E61.trimOffspring", {"start": v(26.8, 10.85) * mm, "end": v(27.8, 10.85) * mm});
            skLineSegment(sketch, "E62.trimOffspring", {"start": v(41.8, 10.85) * mm, "end": v(42.8, 10.85) * mm});
            skSolve(sketch);
        }
        {
            var Q0;
            Q0 = qSketchRegion(id + "F42", true);
            extrude(context, id + "F43", {"entities" : qUnion([Q0]), "operationType" : NewBodyOperationType.ADD, "oppositeDirection" : true, "depth" : 11.5 * mm});
        }
        {
            var Q0;
            Q0=makeQuery(id+"F43.opExtrude","SWEPT_EDGE",EDGE,{"disambiguationData":[OSD([sQuery(id+"F42.wireOp",EDGE,"E54.right"),sQuery(id+"F42.wireOp",EDGE,"E62.trimOffspring")])]});
            var Q1;
            Q1=makeQuery(id+"F43.opExtrude","SWEPT_EDGE",EDGE,{"disambiguationData":[OSD([sQuery(id+"F42.wireOp",EDGE,"E54.top"),sQuery(id+"F42.wireOp",EDGE,"E54.left")])]});
            var Q2;
            Q2=makeQuery(id+"F43.opExtrude","SWEPT_EDGE",EDGE,{"disambiguationData":[OSD([sQuery(id+"F42.wireOp",EDGE,"E53.right"),sQuery(id+"F42.wireOp",EDGE,"E61.trimOffspring")])]});
            var Q3;
            Q3=makeQuery(id+"F43.opExtrude","SWEPT_EDGE",EDGE,{"disambiguationData":[OSD([sQuery(id+"F42.wireOp",EDGE,"E53.top"),sQuery(id+"F42.wireOp",EDGE,"E53.left")])]});
            var Q4;
            Q4=makeQuery(id+"F43.boolean.opBoolean","INTERSECT",EDGE,{"disambiguationData":[OD(0.0)],"derivedFrom":[makeQuery(id+"F17.boolean.opBoolean","MERGE",FACE,{"derivedFrom":[makeQuery(id+"F9.boolean.opBoolean","MERGE",FACE,{"derivedFrom":[makeQuery(id+"F1.opExtrude","SWEPT_FACE",FACE,{"disambiguationData":[OSD([sQuery(id+"F0.wireOp",EDGE,"E0.top")])]}),makeQuery(id+"F9.opExtrude","SWEPT_FACE",FACE,{"disambiguationData":[OSD([sQuery(id+"F8.wireOp",EDGE,"E11.bottom")])]})]}),makeQuery(id+"F17.opExtrude","SWEPT_FACE",FACE,{"disambiguationData":[OSD([sQuery(id+"F16.wireOp",EDGE,"E21.bottom")])]})]}),makeQuery(id+"F43.opExtrude","SWEPT_FACE",FACE,{"disambiguationData":[OSD([sQuery(id+"F42.wireOp",EDGE,"E54.right")])]})]});
            var Q5;
            Q5=makeQuery(id+"F43.boolean.opBoolean","INTERSECT",EDGE,{"disambiguationData":[OD(1.0)],"derivedFrom":[makeQuery(id+"F17.boolean.opBoolean","MERGE",FACE,{"derivedFrom":[makeQuery(id+"F9.boolean.opBoolean","MERGE",FACE,{"derivedFrom":[makeQuery(id+"F1.opExtrude","SWEPT_FACE",FACE,{"disambiguationData":[OSD([sQuery(id+"F0.wireOp",EDGE,"E0.top")])]}),makeQuery(id+"F9.opExtrude","SWEPT_FACE",FACE,{"disambiguationData":[OSD([sQuery(id+"F8.wireOp",EDGE,"E11.bottom")])]})]}),makeQuery(id+"F17.opExtrude","SWEPT_FACE",FACE,{"disambiguationData":[OSD([sQuery(id+"F16.wireOp",EDGE,"E21.bottom")])]})]}),makeQuery(id+"F43.opExtrude","SWEPT_FACE",FACE,{"disambiguationData":[OSD([sQuery(id+"F42.wireOp",EDGE,"E54.right")])]})]});
            var Q6;
            Q6=makeQuery(id+"F43.boolean.opBoolean","INTERSECT",EDGE,{"disambiguationData":[OD(1.0)],"derivedFrom":[makeQuery(id+"F17.boolean.opBoolean","MERGE",FACE,{"derivedFrom":[makeQuery(id+"F9.boolean.opBoolean","MERGE",FACE,{"derivedFrom":[makeQuery(id+"F1.opExtrude","SWEPT_FACE",FACE,{"disambiguationData":[OSD([sQuery(id+"F0.wireOp",EDGE,"E0.top")])]}),makeQuery(id+"F9.opExtrude","SWEPT_FACE",FACE,{"disambiguationData":[OSD([sQuery(id+"F8.wireOp",EDGE,"E11.bottom")])]})]}),makeQuery(id+"F17.opExtrude","SWEPT_FACE",FACE,{"disambiguationData":[OSD([sQuery(id+"F16.wireOp",EDGE,"E21.bottom")])]})]}),makeQuery(id+"F43.opExtrude","SWEPT_FACE",FACE,{"disambiguationData":[OSD([sQuery(id+"F42.wireOp",EDGE,"E53.right")])]})]});
            var Q7;
            Q7=makeQuery(id+"F43.boolean.opBoolean","INTERSECT",EDGE,{"disambiguationData":[OD(0.0)],"derivedFrom":[makeQuery(id+"F17.boolean.opBoolean","MERGE",FACE,{"derivedFrom":[makeQuery(id+"F9.boolean.opBoolean","MERGE",FACE,{"derivedFrom":[makeQuery(id+"F1.opExtrude","SWEPT_FACE",FACE,{"disambiguationData":[OSD([sQuery(id+"F0.wireOp",EDGE,"E0.top")])]}),makeQuery(id+"F9.opExtrude","SWEPT_FACE",FACE,{"disambiguationData":[OSD([sQuery(id+"F8.wireOp",EDGE,"E11.bottom")])]})]}),makeQuery(id+"F17.opExtrude","SWEPT_FACE",FACE,{"disambiguationData":[OSD([sQuery(id+"F16.wireOp",EDGE,"E21.bottom")])]})]}),makeQuery(id+"F43.opExtrude","SWEPT_FACE",FACE,{"disambiguationData":[OSD([sQuery(id+"F42.wireOp",EDGE,"E53.right")])]})]});
            var Q8;
            Q8=makeQuery(id+"F43.boolean.opBoolean","INTERSECT",EDGE,{"disambiguationData":[OD(0.0)],"derivedFrom":[makeQuery(id+"F17.boolean.opBoolean","MERGE",FACE,{"derivedFrom":[makeQuery(id+"F9.boolean.opBoolean","MERGE",FACE,{"derivedFrom":[makeQuery(id+"F1.opExtrude","SWEPT_FACE",FACE,{"disambiguationData":[OSD([sQuery(id+"F0.wireOp",EDGE,"E0.top")])]}),makeQuery(id+"F9.opExtrude","SWEPT_FACE",FACE,{"disambiguationData":[OSD([sQuery(id+"F8.wireOp",EDGE,"E11.bottom")])]})]}),makeQuery(id+"F17.opExtrude","SWEPT_FACE",FACE,{"disambiguationData":[OSD([sQuery(id+"F16.wireOp",EDGE,"E21.bottom")])]})]}),makeQuery(id+"F43.opExtrude","SWEPT_FACE",FACE,{"disambiguationData":[OSD([sQuery(id+"F42.wireOp",EDGE,"E53.left")])]})]});
            var Q9;
            Q9=makeQuery(id+"F43.boolean.opBoolean","INTERSECT",EDGE,{"disambiguationData":[OD(1.0)],"derivedFrom":[makeQuery(id+"F17.boolean.opBoolean","MERGE",FACE,{"derivedFrom":[makeQuery(id+"F9.boolean.opBoolean","MERGE",FACE,{"derivedFrom":[makeQuery(id+"F1.opExtrude","SWEPT_FACE",FACE,{"disambiguationData":[OSD([sQuery(id+"F0.wireOp",EDGE,"E0.top")])]}),makeQuery(id+"F9.opExtrude","SWEPT_FACE",FACE,{"disambiguationData":[OSD([sQuery(id+"F8.wireOp",EDGE,"E11.bottom")])]})]}),makeQuery(id+"F17.opExtrude","SWEPT_FACE",FACE,{"disambiguationData":[OSD([sQuery(id+"F16.wireOp",EDGE,"E21.bottom")])]})]}),makeQuery(id+"F43.opExtrude","SWEPT_FACE",FACE,{"disambiguationData":[OSD([sQuery(id+"F42.wireOp",EDGE,"E53.left")])]})]});
            var Q10;
            Q10=makeQuery(id+"F43.boolean.opBoolean","INTERSECT",EDGE,{"disambiguationData":[OD(0.0)],"derivedFrom":[makeQuery(id+"F17.boolean.opBoolean","MERGE",FACE,{"derivedFrom":[makeQuery(id+"F9.boolean.opBoolean","MERGE",FACE,{"derivedFrom":[makeQuery(id+"F1.opExtrude","SWEPT_FACE",FACE,{"disambiguationData":[OSD([sQuery(id+"F0.wireOp",EDGE,"E0.top")])]}),makeQuery(id+"F9.opExtrude","SWEPT_FACE",FACE,{"disambiguationData":[OSD([sQuery(id+"F8.wireOp",EDGE,"E11.bottom")])]})]}),makeQuery(id+"F17.opExtrude","SWEPT_FACE",FACE,{"disambiguationData":[OSD([sQuery(id+"F16.wireOp",EDGE,"E21.bottom")])]})]}),makeQuery(id+"F43.opExtrude","SWEPT_FACE",FACE,{"disambiguationData":[OSD([sQuery(id+"F42.wireOp",EDGE,"E54.left")])]})]});
            var Q11;
            Q11=makeQuery(id+"F43.boolean.opBoolean","INTERSECT",EDGE,{"disambiguationData":[OD(1.0)],"derivedFrom":[makeQuery(id+"F17.boolean.opBoolean","MERGE",FACE,{"derivedFrom":[makeQuery(id+"F9.boolean.opBoolean","MERGE",FACE,{"derivedFrom":[makeQuery(id+"F1.opExtrude","SWEPT_FACE",FACE,{"disambiguationData":[OSD([sQuery(id+"F0.wireOp",EDGE,"E0.top")])]}),makeQuery(id+"F9.opExtrude","SWEPT_FACE",FACE,{"disambiguationData":[OSD([sQuery(id+"F8.wireOp",EDGE,"E11.bottom")])]})]}),makeQuery(id+"F17.opExtrude","SWEPT_FACE",FACE,{"disambiguationData":[OSD([sQuery(id+"F16.wireOp",EDGE,"E21.bottom")])]})]}),makeQuery(id+"F43.opExtrude","SWEPT_FACE",FACE,{"disambiguationData":[OSD([sQuery(id+"F42.wireOp",EDGE,"E54.left")])]})]});
            fillet(context, id + "F44", {"entities" : qUnion([Q0, Q1, Q2, Q3, Q4, Q5, Q6, Q7, Q8, Q9, Q10, Q11]), "radius" : 0.3 * mm, "tangentPropagation" : true, "allowEdgeOverflow" : false});
        }
        {
            var Q0;
            Q0=makeQuery(id+"F43.opExtrude","SWEPT_FACE",FACE,{"disambiguationData":[OSD([sQuery(id+"F42.wireOp",EDGE,"E59")])]});
            var sketch = newSketch(context, id + "F45", { "sketchPlane" : qUnion([Q0])});
            skLineSegment(sketch, "E63.bottom", {"start": v(39.8, 3.68) * mm, "end": v(41.8, 3.68) * mm});
            skLineSegment(sketch, "E63.top", {"start": v(39.8, -3.49) * mm, "end": v(41.8, -3.49) * mm});
            skLineSegment(sketch, "E63.left", {"start": v(39.8, 3.68) * mm, "end": v(39.8, -3.49) * mm});
            skLineSegment(sketch, "E63.right", {"start": v(41.8, 3.68) * mm, "end": v(41.8, -3.49) * mm});
            skSolve(sketch);
        }
        {
            var Q0;
            Q0 = qSketchRegion(id + "F45", true);
            extrude(context, id + "F46", {"entities" : qUnion([Q0]), "operationType" : NewBodyOperationType.REMOVE, "endBound" : BoundingType.THROUGH_ALL, "oppositeDirection" : true, "depth" : 25 * mm, "offsetDistance" : 25 * mm});
        }
        {
            var Q0;
            Q0=makeQuery(id+"F43.opExtrude","SWEPT_FACE",FACE,{"disambiguationData":[OSD([sQuery(id+"F42.wireOp",EDGE,"E56")])]});
            var sketch = newSketch(context, id + "F47", { "sketchPlane" : qUnion([Q0])});
            skLineSegment(sketch, "E64.bottom", {"start": v(24.8, 3.7) * mm, "end": v(26.8, 3.7) * mm});
            skLineSegment(sketch, "E64.top", {"start": v(24.8, -3.7) * mm, "end": v(26.8, -3.7) * mm});
            skLineSegment(sketch, "E64.left", {"start": v(24.8, 3.7) * mm, "end": v(24.8, -3.7) * mm});
            skLineSegment(sketch, "E64.right", {"start": v(26.8, 3.7) * mm, "end": v(26.8, -3.7) * mm});
            skSolve(sketch);
        }
        {
            var Q0;
            Q0 = qSketchRegion(id + "F47", true);
            extrude(context, id + "F48", {"entities" : qUnion([Q0]), "operationType" : NewBodyOperationType.REMOVE, "oppositeDirection" : true, "depth" : 6 * mm, "offsetDistance" : 25 * mm});
        }
        {
            var Q0;
            Q0=makeQuery(id+"F1.opExtrude","SWEPT_FACE",FACE,{"disambiguationData":[OSD([sQuery(id+"F0.wireOp",EDGE,"E0.right")])]});
            var sketch = newSketch(context, id + "F49", { "sketchPlane" : qUnion([Q0])});
            skLineSegment(sketch, "E65.bottom", {"start": v(-4.8, 5.83) * mm, "end": v(4.8, 5.83) * mm});
            skLineSegment(sketch, "E65.top", {"start": v(-4.8, 4.23) * mm, "end": v(4.8, 4.23) * mm});
            skLineSegment(sketch, "E65.left", {"start": v(-4.8, 5.83) * mm, "end": v(-4.8, 4.23) * mm});
            skLineSegment(sketch, "E65.right", {"start": v(4.8, 5.83) * mm, "end": v(4.8, 4.23) * mm});
            skSolve(sketch);
        }
        {
            var Q0;
            Q0 = qSketchRegion(id + "F49", true);
            extrude(context, id + "F50", {"entities" : qUnion([Q0]), "operationType" : NewBodyOperationType.REMOVE, "oppositeDirection" : true, "depth" : 18 * mm, "offsetDistance" : 25 * mm});
        }
        {
            var Q0;
            Q0=makeQuery(id+"F28.opExtrude","SWEPT_FACE",FACE,{"disambiguationData":[OSD([sQuery(id+"F27.wireOp",EDGE,"E38"),sQuery(id+"F27.wireOp",EDGE,"E39")])]});
            var sketch = newSketch(context, id + "F51", { "sketchPlane" : qUnion([Q0])});
            skLineSegment(sketch, "E66.bottom", {"start": v(-37, 4.7) * mm, "end": v(-26, 4.7) * mm});
            skLineSegment(sketch, "E66.top", {"start": v(-37, -4.7) * mm, "end": v(-26, -4.7) * mm});
            skLineSegment(sketch, "E66.left", {"start": v(-37, 4.7) * mm, "end": v(-37, -4.7) * mm});
            skLineSegment(sketch, "E66.right", {"start": v(-26, 4.7) * mm, "end": v(-26, -4.7) * mm});
            skSolve(sketch);
        }
        {
            var Q0;
            Q0 = qSketchRegion(id + "F51", true);
            extrude(context, id + "F52", {"entities" : qUnion([Q0]), "operationType" : NewBodyOperationType.REMOVE, "oppositeDirection" : true, "depth" : 2 * mm, "offsetDistance" : 25 * mm});
        }
        {
            var Q0;
            Q0=makeQuery(id+"F52.boolean.opBoolean","COPY",FACE,{"derivedFrom":makeQuery(id+"F52.opExtrude","CAP_FACE",FACE,{"disambiguationData":[OSD([sQuery(id+"F51.wireOp",EDGE,"E66.bottom"),sQuery(id+"F51.wireOp",EDGE,"E66.top"),sQuery(id+"F51.wireOp",EDGE,"E66.left"),sQuery(id+"F51.wireOp",EDGE,"E66.right")])],"isStart":false})});
            var sketch = newSketch(context, id + "F53", { "sketchPlane" : qUnion([Q0])});
            skLineSegment(sketch, "E67.bottom", {"start": v(-37, 4) * mm, "end": v(-32, 4) * mm});
            skLineSegment(sketch, "E67.top", {"start": v(-37, -4) * mm, "end": v(-32, -4) * mm});
            skLineSegment(sketch, "E67.left", {"start": v(-37, 4) * mm, "end": v(-37, -4) * mm});
            skLineSegment(sketch, "E67.right", {"start": v(-32, 4) * mm, "end": v(-32, -4) * mm});
            skSolve(sketch);
        }
        {
            var Q0;
            Q0 = qSketchRegion(id + "F53", true);
            extrude(context, id + "F54", {"entities" : qUnion([Q0]), "operationType" : NewBodyOperationType.REMOVE, "oppositeDirection" : true, "depth" : 6.5 * mm, "offsetDistance" : 25 * mm});
        }
        {
            var Q0;
            {var subQ2=sQuery(id+"F31.wireOp",EDGE,"E44");var subQ4=sQuery(id+"F0.wireOp",EDGE,"E0.left");Q0=makeQuery(id+"F54.boolean.opBoolean","SPLIT",FACE,{"disambiguationData":[TD([makeQuery(id+"F34.boolean.opBoolean","COPY",FACE,{"derivedFrom":makeQuery(id+"F34.opExtrude","SWEPT_FACE",FACE,{"disambiguationData":[OSD([sQuery(id+"F33.wireOp",EDGE,"E49")])]})})])],"derivedFrom":makeQuery(id+"F32.boolean.opBoolean","MERGE",FACE,{"derivedFrom":[makeQuery(id+"F1.opExtrude","SWEPT_FACE",FACE,{"disambiguationData":[OSD([subQ4])]}),makeQuery(id+"F32.opExtrude","SWEPT_FACE",FACE,{"disambiguationData":[OSD([subQ2])]})]})});}
            var Q1;
            {var subQ0=sQuery(id+"F0.wireOp",EDGE,"E0.left");var subQ5=sQuery(id+"F31.wireOp",EDGE,"E44");Q1=makeQuery(id+"F54.boolean.opBoolean","SPLIT",FACE,{"disambiguationData":[TD([makeQuery(id+"F34.boolean.opBoolean","COPY",FACE,{"derivedFrom":makeQuery(id+"F34.opExtrude","SWEPT_FACE",FACE,{"disambiguationData":[OSD([sQuery(id+"F33.wireOp",EDGE,"E47")])]})})])],"derivedFrom":makeQuery(id+"F32.boolean.opBoolean","MERGE",FACE,{"derivedFrom":[makeQuery(id+"F1.opExtrude","SWEPT_FACE",FACE,{"disambiguationData":[OSD([subQ0])]}),makeQuery(id+"F32.opExtrude","SWEPT_FACE",FACE,{"disambiguationData":[OSD([subQ5])]})]})});}
            extrude(context, id + "F55", {"entities" : qUnion([Q0, Q1]), "operationType" : NewBodyOperationType.ADD, "depth" : 1 * mm, "offsetDistance" : 25 * mm});
        }
        {
            var Q0;
            {var subQ2=sQuery(id+"F51.wireOp",EDGE,"E66.bottom");var subQ3=sQuery(id+"F27.wireOp",EDGE,"E40");Q0=makeQuery(id+"F52.boolean.opBoolean","SPLIT",FACE,{"disambiguationData":[TD([makeQuery(id+"F52.opExtrude","SWEPT_FACE",FACE,{"disambiguationData":[OSD([subQ2])]})])],"derivedFrom":makeQuery(id+"F28.opExtrude","SWEPT_FACE",FACE,{"disambiguationData":[OSD([subQ3])]})});}
            var Q1;
            {var subQ2=sQuery(id+"F27.wireOp",EDGE,"E40");var subQ6=sQuery(id+"F51.wireOp",EDGE,"E66.top");Q1=makeQuery(id+"F52.boolean.opBoolean","SPLIT",FACE,{"disambiguationData":[TD([makeQuery(id+"F52.opExtrude","SWEPT_FACE",FACE,{"disambiguationData":[OSD([subQ6])]})])],"derivedFrom":makeQuery(id+"F28.opExtrude","SWEPT_FACE",FACE,{"disambiguationData":[OSD([subQ2])]})});}
            extrude(context, id + "F56", {"entities" : qUnion([Q0, Q1]), "operationType" : NewBodyOperationType.ADD, "depth" : 1 * mm, "offsetDistance" : 25 * mm});
        }
        {
            var Q0;
            Q0=makeQuery(id+"F28.opExtrude","SWEPT_FACE",FACE,{"disambiguationData":[OSD([sQuery(id+"F27.wireOp",EDGE,"E38"),sQuery(id+"F27.wireOp",EDGE,"E39")])]});
            extrude(context, id + "F57", {"entities" : qUnion([Q0]), "operationType" : NewBodyOperationType.ADD, "depth" : 2 * mm, "offsetDistance" : 25 * mm});
        }
        {
            var Q0;
            Q0=makeQuery(id+"F28.opExtrude","SWEPT_FACE",FACE,{"disambiguationData":[OSD([sQuery(id+"F27.wireOp",EDGE,"E37")])]});
            extrude(context, id + "F58", {"entities" : qUnion([Q0]), "operationType" : NewBodyOperationType.ADD, "depth" : 2 * mm, "offsetDistance" : 25 * mm});
        }
        {
            var Q0;
            Q0=makeQuery(id+"F28.opExtrude","SWEPT_FACE",FACE,{"disambiguationData":[OSD([sQuery(id+"F27.wireOp",EDGE,"E35")])]});
            extrude(context, id + "F59", {"entities" : qUnion([Q0]), "operationType" : NewBodyOperationType.ADD, "depth" : 1 * mm, "offsetDistance" : 25 * mm});
        }
        {
            var Q0;
            {var subQ0=sQuery(id+"F27.wireOp",EDGE,"E34");Q0=makeQuery(id+"F59.boolean.opBoolean","MERGE",FACE,{"derivedFrom":[makeQuery(id+"F28.opExtrude","SWEPT_FACE",FACE,{"disambiguationData":[OSD([subQ0])]}),makeQuery(id+"F59.opExtrude","SWEPT_FACE",FACE,{"disambiguationData":[OSD([subQ0,sQuery(id+"F27.wireOp",EDGE,"E35")])]})]});}
            extrude(context, id + "F60", {"entities" : qUnion([Q0]), "operationType" : NewBodyOperationType.ADD, "depth" : 1 * mm, "offsetDistance" : 25 * mm});
        }
        {
            var Q0;
            {var subQ0=sQuery(id+"F27.wireOp",EDGE,"E35");var subQ1=sQuery(id+"F27.wireOp",EDGE,"E34");var subQ2=sQuery(id+"F27.wireOp",EDGE,"E37");var subQ3=sQuery(id+"F27.wireOp",EDGE,"E39");var subQ4=sQuery(id+"F27.wireOp",EDGE,"E38");var subQ5=sQuery(id+"F27.wireOp",EDGE,"E40");var subQ6=sQuery(id+"F31.wireOp",EDGE,"E44");var subQ7=sQuery(id+"F0.wireOp",EDGE,"E0.left");var subQ8=sQuery(id+"F0.wireOp",EDGE,"E0.top");Q0=makeQuery(id+"F60.boolean.opBoolean","MERGE",FACE,{"derivedFrom":[makeQuery(id+"F59.boolean.opBoolean","MERGE",FACE,{"derivedFrom":[makeQuery(id+"F58.boolean.opBoolean","MERGE",FACE,{"derivedFrom":[makeQuery(id+"F57.boolean.opBoolean","MERGE",FACE,{"derivedFrom":[makeQuery(id+"F56.boolean.opBoolean","MERGE",FACE,{"derivedFrom":[makeQuery(id+"F55.boolean.opBoolean","MERGE",FACE,{"derivedFrom":[makeQuery(id+"F43.boolean.opBoolean","MERGE",FACE,{"derivedFrom":[makeQuery(id+"F32.boolean.opBoolean","MERGE",FACE,{"derivedFrom":[makeQuery(id+"F28.boolean.opBoolean","MERGE",FACE,{"derivedFrom":[makeQuery(id+"F1.opExtrude","CAP_FACE",FACE,{"disambiguationData":[OSD([sQuery(id+"F0.wireOp",EDGE,"E0.bottom"),subQ8,subQ7,sQuery(id+"F0.wireOp",EDGE,"E0.right"),sQuery(id+"F0.wireOp",EDGE,"E1"),sQuery(id+"F0.wireOp",EDGE,"E2"),sQuery(id+"F0.wireOp",EDGE,"E3")])],"isStart":false}),makeQuery(id+"F28.opExtrude","CAP_FACE",FACE,{"disambiguationData":[OSD([subQ8,sQuery(id+"F27.wireOp",EDGE,"E32"),sQuery(id+"F27.wireOp",EDGE,"E33"),subQ1,subQ0,sQuery(id+"F27.wireOp",EDGE,"E36"),subQ2,subQ4,subQ3,subQ5])],"isStart":true})]}),makeQuery(id+"F32.opExtrude","CAP_FACE",FACE,{"disambiguationData":[OSD([sQuery(id+"F18.wireOp",EDGE,"E23"),subQ6,sQuery(id+"F31.wireOp",EDGE,"E45"),sQuery(id+"F31.wireOp",EDGE,"E46")])],"isStart":true})]}),makeQuery(id+"F43.opExtrude","CAP_FACE",FACE,{"disambiguationData":[OSD([sQuery(id+"F42.wireOp",EDGE,"E53.bottom"),sQuery(id+"F42.wireOp",EDGE,"E53.top"),sQuery(id+"F42.wireOp",EDGE,"E53.left"),sQuery(id+"F42.wireOp",EDGE,"E53.right"),sQuery(id+"F42.wireOp",EDGE,"E55"),sQuery(id+"F42.wireOp",EDGE,"E56"),sQuery(id+"F42.wireOp",EDGE,"E57"),sQuery(id+"F42.wireOp",EDGE,"E61.trimOffspring")])],"isStart":true}),makeQuery(id+"F43.opExtrude","CAP_FACE",FACE,{"disambiguationData":[OSD([sQuery(id+"F42.wireOp",EDGE,"E54.bottom"),sQuery(id+"F42.wireOp",EDGE,"E54.top"),sQuery(id+"F42.wireOp",EDGE,"E54.left"),sQuery(id+"F42.wireOp",EDGE,"E54.right"),sQuery(id+"F42.wireOp",EDGE,"E58"),sQuery(id+"F42.wireOp",EDGE,"E59"),sQuery(id+"F42.wireOp",EDGE,"E60"),sQuery(id+"F42.wireOp",EDGE,"E62.trimOffspring")])],"isStart":true})]}),makeQuery(id+"F55.opExtrude","SWEPT_FACE",FACE,{"disambiguationData":[OSD([subQ7,subQ6]),TDD([makeQuery(id+"F32.boolean.opBoolean","MERGE",EDGE,{"derivedFrom":[makeQuery(id+"F1.opExtrude","CAP_EDGE",EDGE,{"disambiguationData":[OSD([subQ7])],"isStart":false}),makeQuery(id+"F32.opExtrude","CAP_EDGE",EDGE,{"disambiguationData":[OSD([subQ6])],"isStart":true})]})])]})]}),makeQuery(id+"F56.opExtrude","SWEPT_FACE",FACE,{"disambiguationData":[OSD([subQ5]),TDD([makeQuery(id+"F28.opExtrude","CAP_EDGE",EDGE,{"disambiguationData":[OSD([subQ5])],"isStart":true})])]})]}),makeQuery(id+"F57.opExtrude","SWEPT_FACE",FACE,{"disambiguationData":[OSD([subQ4,subQ3]),TDD([makeQuery(id+"F28.opExtrude","CAP_EDGE",EDGE,{"disambiguationData":[OSD([subQ4,subQ3])],"isStart":true})])]})]}),makeQuery(id+"F58.opExtrude","SWEPT_FACE",FACE,{"disambiguationData":[OSD([subQ2]),TDD([makeQuery(id+"F28.opExtrude","CAP_EDGE",EDGE,{"disambiguationData":[OSD([subQ2])],"isStart":true})])]})]}),makeQuery(id+"F59.opExtrude","SWEPT_FACE",FACE,{"disambiguationData":[OSD([subQ0]),TDD([makeQuery(id+"F28.opExtrude","CAP_EDGE",EDGE,{"disambiguationData":[OSD([subQ0])],"isStart":true})])]})]}),makeQuery(id+"F60.opExtrude","SWEPT_FACE",FACE,{"disambiguationData":[OSD([subQ1,subQ0]),TDD([makeQuery(id+"F59.boolean.opBoolean","MERGE",EDGE,{"derivedFrom":[makeQuery(id+"F28.opExtrude","CAP_EDGE",EDGE,{"disambiguationData":[OSD([subQ1])],"isStart":true}),makeQuery(id+"F59.opExtrude","SWEPT_EDGE",EDGE,{"disambiguationData":[OSD([subQ1,subQ0]),TDD([makeQuery(id+"F28.opExtrude","CAP_VERTEX",VERTEX,{"disambiguationData":[OSD([subQ1,subQ0])],"isStart":true})])]})]})])]})]});}
            var sketch = newSketch(context, id + "F61", { "sketchPlane" : qUnion([Q0])});
            skLineSegment(sketch, "E68", {"start": v(-23.82, 14.33) * mm, "end": v(-26.1, 15.33) * mm});
            skLineSegment(sketch, "E69", {"start": v(-26.1, 15.33) * mm, "end": v(-23.82, 15.33) * mm});
            skLineSegment(sketch, "E70", {"start": v(-23.82, 15.33) * mm, "end": v(-23.82, 14.33) * mm});
            skSolve(sketch);
        }
        {
            var Q0;
            Q0=makeQuery(id+"F61.imprint","IMPRINT",FACE,{"disambiguationData":[TD([[makeQuery(id+"F61.imprint","IMPRINT",EDGE,{"derivedFrom":sQuery(id+"F61.wireOp",EDGE,"E68")}),-1.0]])]});
            extrude(context, id + "F62", {"entities" : qUnion([Q0]), "operationType" : NewBodyOperationType.REMOVE, "endBound" : BoundingType.THROUGH_ALL, "oppositeDirection" : true, "depth" : 25 * mm, "offsetDistance" : 25 * mm});
        }
        {
            var Q0;
            {var subQ0=sQuery(id+"F27.wireOp",EDGE,"E35");var subQ1=sQuery(id+"F27.wireOp",EDGE,"E34");var subQ2=sQuery(id+"F27.wireOp",EDGE,"E37");var subQ3=sQuery(id+"F27.wireOp",EDGE,"E39");var subQ4=sQuery(id+"F27.wireOp",EDGE,"E38");var subQ5=sQuery(id+"F27.wireOp",EDGE,"E40");var subQ6=sQuery(id+"F31.wireOp",EDGE,"E44");var subQ7=sQuery(id+"F0.wireOp",EDGE,"E0.left");var subQ8=sQuery(id+"F0.wireOp",EDGE,"E0.top");Q0=makeQuery(id+"F60.boolean.opBoolean","MERGE",FACE,{"derivedFrom":[makeQuery(id+"F59.boolean.opBoolean","MERGE",FACE,{"derivedFrom":[makeQuery(id+"F58.boolean.opBoolean","MERGE",FACE,{"derivedFrom":[makeQuery(id+"F57.boolean.opBoolean","MERGE",FACE,{"derivedFrom":[makeQuery(id+"F56.boolean.opBoolean","MERGE",FACE,{"derivedFrom":[makeQuery(id+"F55.boolean.opBoolean","MERGE",FACE,{"derivedFrom":[makeQuery(id+"F43.boolean.opBoolean","MERGE",FACE,{"derivedFrom":[makeQuery(id+"F32.boolean.opBoolean","MERGE",FACE,{"derivedFrom":[makeQuery(id+"F28.boolean.opBoolean","MERGE",FACE,{"derivedFrom":[makeQuery(id+"F1.opExtrude","CAP_FACE",FACE,{"disambiguationData":[OSD([sQuery(id+"F0.wireOp",EDGE,"E0.bottom"),subQ8,subQ7,sQuery(id+"F0.wireOp",EDGE,"E0.right"),sQuery(id+"F0.wireOp",EDGE,"E1"),sQuery(id+"F0.wireOp",EDGE,"E2"),sQuery(id+"F0.wireOp",EDGE,"E3")])],"isStart":false}),makeQuery(id+"F28.opExtrude","CAP_FACE",FACE,{"disambiguationData":[OSD([subQ8,sQuery(id+"F27.wireOp",EDGE,"E32"),sQuery(id+"F27.wireOp",EDGE,"E33"),subQ1,subQ0,sQuery(id+"F27.wireOp",EDGE,"E36"),subQ2,subQ4,subQ3,subQ5])],"isStart":true})]}),makeQuery(id+"F32.opExtrude","CAP_FACE",FACE,{"disambiguationData":[OSD([sQuery(id+"F18.wireOp",EDGE,"E23"),subQ6,sQuery(id+"F31.wireOp",EDGE,"E45"),sQuery(id+"F31.wireOp",EDGE,"E46")])],"isStart":true})]}),makeQuery(id+"F43.opExtrude","CAP_FACE",FACE,{"disambiguationData":[OSD([sQuery(id+"F42.wireOp",EDGE,"E53.bottom"),sQuery(id+"F42.wireOp",EDGE,"E53.top"),sQuery(id+"F42.wireOp",EDGE,"E53.left"),sQuery(id+"F42.wireOp",EDGE,"E53.right"),sQuery(id+"F42.wireOp",EDGE,"E55"),sQuery(id+"F42.wireOp",EDGE,"E56"),sQuery(id+"F42.wireOp",EDGE,"E57"),sQuery(id+"F42.wireOp",EDGE,"E61.trimOffspring")])],"isStart":true}),makeQuery(id+"F43.opExtrude","CAP_FACE",FACE,{"disambiguationData":[OSD([sQuery(id+"F42.wireOp",EDGE,"E54.bottom"),sQuery(id+"F42.wireOp",EDGE,"E54.top"),sQuery(id+"F42.wireOp",EDGE,"E54.left"),sQuery(id+"F42.wireOp",EDGE,"E54.right"),sQuery(id+"F42.wireOp",EDGE,"E58"),sQuery(id+"F42.wireOp",EDGE,"E59"),sQuery(id+"F42.wireOp",EDGE,"E60"),sQuery(id+"F42.wireOp",EDGE,"E62.trimOffspring")])],"isStart":true})]}),makeQuery(id+"F55.opExtrude","SWEPT_FACE",FACE,{"disambiguationData":[OSD([subQ7,subQ6]),TDD([makeQuery(id+"F32.boolean.opBoolean","MERGE",EDGE,{"derivedFrom":[makeQuery(id+"F1.opExtrude","CAP_EDGE",EDGE,{"disambiguationData":[OSD([subQ7])],"isStart":false}),makeQuery(id+"F32.opExtrude","CAP_EDGE",EDGE,{"disambiguationData":[OSD([subQ6])],"isStart":true})]})])]})]}),makeQuery(id+"F56.opExtrude","SWEPT_FACE",FACE,{"disambiguationData":[OSD([subQ5]),TDD([makeQuery(id+"F28.opExtrude","CAP_EDGE",EDGE,{"disambiguationData":[OSD([subQ5])],"isStart":true})])]})]}),makeQuery(id+"F57.opExtrude","SWEPT_FACE",FACE,{"disambiguationData":[OSD([subQ4,subQ3]),TDD([makeQuery(id+"F28.opExtrude","CAP_EDGE",EDGE,{"disambiguationData":[OSD([subQ4,subQ3])],"isStart":true})])]})]}),makeQuery(id+"F58.opExtrude","SWEPT_FACE",FACE,{"disambiguationData":[OSD([subQ2]),TDD([makeQuery(id+"F28.opExtrude","CAP_EDGE",EDGE,{"disambiguationData":[OSD([subQ2])],"isStart":true})])]})]}),makeQuery(id+"F59.opExtrude","SWEPT_FACE",FACE,{"disambiguationData":[OSD([subQ0]),TDD([makeQuery(id+"F28.opExtrude","CAP_EDGE",EDGE,{"disambiguationData":[OSD([subQ0])],"isStart":true})])]})]}),makeQuery(id+"F60.opExtrude","SWEPT_FACE",FACE,{"disambiguationData":[OSD([subQ1,subQ0]),TDD([makeQuery(id+"F59.boolean.opBoolean","MERGE",EDGE,{"derivedFrom":[makeQuery(id+"F28.opExtrude","CAP_EDGE",EDGE,{"disambiguationData":[OSD([subQ1])],"isStart":true}),makeQuery(id+"F59.opExtrude","SWEPT_EDGE",EDGE,{"disambiguationData":[OSD([subQ1,subQ0]),TDD([makeQuery(id+"F28.opExtrude","CAP_VERTEX",VERTEX,{"disambiguationData":[OSD([subQ1,subQ0])],"isStart":true})])]})]})])]})]});}
            var sketch = newSketch(context, id + "F63", { "sketchPlane" : qUnion([Q0])});
            skLineSegment(sketch, "E71.bottom", {"start": v(-26.75, 12.33) * mm, "end": v(-29.8, 12.33) * mm});
            skLineSegment(sketch, "E71.top", {"start": v(-26.75, 13.33) * mm, "end": v(-29.8, 13.33) * mm});
            skLineSegment(sketch, "E71.left", {"start": v(-26.75, 12.33) * mm, "end": v(-26.75, 13.33) * mm});
            skLineSegment(sketch, "E71.right", {"start": v(-29.8, 12.33) * mm, "end": v(-29.8, 13.33) * mm});
            skSolve(sketch);
        }
        {
            var Q0;
            Q0=makeQuery(id+"F63.imprint","IMPRINT",FACE,{"disambiguationData":[TD([[makeQuery(id+"F63.imprint","IMPRINT",EDGE,{"derivedFrom":sQuery(id+"F63.wireOp",EDGE,"E71.bottom")}),1.0]])]});
            extrude(context, id + "F64", {"entities" : qUnion([Q0]), "operationType" : NewBodyOperationType.REMOVE, "endBound" : BoundingType.THROUGH_ALL, "oppositeDirection" : true, "depth" : 25 * mm, "offsetDistance" : 25 * mm});
        }
        {
            var Q0;
            {var subQ0=sQuery(id+"F27.wireOp",EDGE,"E40");var subQ1=sQuery(id+"F27.wireOp",EDGE,"E39");var subQ4=makeQuery(id+"F52.boolean.opBoolean","SPLIT",EDGE,{"disambiguationData":[TD([makeQuery(id+"F52.opExtrude","SWEPT_FACE",FACE,{"disambiguationData":[OSD([sQuery(id+"F51.wireOp",EDGE,"E66.top")])]})])],"derivedFrom":makeQuery(id+"F28.opExtrude","SWEPT_EDGE",EDGE,{"disambiguationData":[OSD([subQ1,subQ0])]})});Q0=makeQuery(id+"F57.opExtrude","SWEPT_FACE",FACE,{"disambiguationData":[OSD([subQ1,subQ0]),TDD([makeQuery(id+"F56.boolean.opBoolean","MERGE",EDGE,{"derivedFrom":[subQ4,makeQuery(id+"F56.opExtrude","CAP_EDGE",EDGE,{"disambiguationData":[OSD([subQ1,subQ0]),TDD([subQ4])],"isStart":true})]})])]});}
            var Q1;
            {var subQ0=sQuery(id+"F27.wireOp",EDGE,"E39");var subQ2=sQuery(id+"F27.wireOp",EDGE,"E40");var subQ4=makeQuery(id+"F52.boolean.opBoolean","SPLIT",EDGE,{"disambiguationData":[TD([makeQuery(id+"F52.opExtrude","SWEPT_FACE",FACE,{"disambiguationData":[OSD([sQuery(id+"F51.wireOp",EDGE,"E66.bottom")])]})])],"derivedFrom":makeQuery(id+"F28.opExtrude","SWEPT_EDGE",EDGE,{"disambiguationData":[OSD([subQ0,subQ2])]})});Q1=makeQuery(id+"F57.opExtrude","SWEPT_FACE",FACE,{"disambiguationData":[OSD([subQ0,subQ2]),TDD([makeQuery(id+"F56.boolean.opBoolean","MERGE",EDGE,{"derivedFrom":[subQ4,makeQuery(id+"F56.opExtrude","CAP_EDGE",EDGE,{"disambiguationData":[OSD([subQ0,subQ2]),TDD([subQ4])],"isStart":true})]})])]});}
            extrude(context, id + "F65", {"entities" : qUnion([Q0, Q1]), "operationType" : NewBodyOperationType.ADD, "depth" : 1 * mm, "offsetDistance" : 25 * mm});
        }
        {
            var Q0;
            Q0=makeQuery(id+"F43.opExtrude","SWEPT_FACE",FACE,{"disambiguationData":[OSD([sQuery(id+"F42.wireOp",EDGE,"E53.left")])]});
            var sketch = newSketch(context, id + "F66", { "sketchPlane" : qUnion([Q0])});
            skLineSegment(sketch, "E72.bottom", {"start": v(4.81, 5.07) * mm, "end": v(-4.69, 5.07) * mm});
            skLineSegment(sketch, "E72.top", {"start": v(4.81, 7.63) * mm, "end": v(-4.69, 7.63) * mm});
            skLineSegment(sketch, "E72.left", {"start": v(4.81, 5.07) * mm, "end": v(4.81, 7.63) * mm});
            skLineSegment(sketch, "E72.right", {"start": v(-4.69, 5.07) * mm, "end": v(-4.69, 7.63) * mm});
            skSolve(sketch);
        }
        {
            var Q0;
            Q0=makeQuery(id+"F66.imprint","IMPRINT",FACE,{"disambiguationData":[TD([[makeQuery(id+"F66.imprint","IMPRINT",EDGE,{"derivedFrom":sQuery(id+"F66.wireOp",EDGE,"E72.bottom")}),1.0]])]});
            extrude(context, id + "F67", {"entities" : qUnion([Q0]), "operationType" : NewBodyOperationType.REMOVE, "oppositeDirection" : true, "depth" : 2 * mm, "offsetDistance" : 25 * mm});
        }
        {
            var Q0;
            Q0=makeQuery(id+"F48.boolean.opBoolean","MERGE",FACE,{"derivedFrom":[makeQuery(id+"F43.opExtrude","SWEPT_FACE",FACE,{"disambiguationData":[OSD([sQuery(id+"F42.wireOp",EDGE,"E55")])]})],"fromTools":[makeQuery(id+"F48.opExtrude","SWEPT_FACE",FACE,{"disambiguationData":[OSD([sQuery(id+"F47.wireOp",EDGE,"E64.left")])]})]});
            var sketch = newSketch(context, id + "F68", { "sketchPlane" : qUnion([Q0])});
            skLineSegment(sketch, "E73.bottom", {"start": v(3.57, 10.85) * mm, "end": v(-3.7, 10.85) * mm});
            skLineSegment(sketch, "E73.top", {"start": v(3.57, 8.35) * mm, "end": v(-3.7, 8.35) * mm});
            skLineSegment(sketch, "E73.left", {"start": v(3.57, 10.85) * mm, "end": v(3.57, 8.35) * mm});
            skLineSegment(sketch, "E73.right", {"start": v(-3.7, 10.85) * mm, "end": v(-3.7, 8.35) * mm});
            skLineSegment(sketch, "E74.bottom", {"start": v(3.7, 8.35) * mm, "end": v(-3.7, 8.35) * mm});
            skLineSegment(sketch, "E74.top", {"start": v(3.7, 7.63) * mm, "end": v(-3.7, 7.63) * mm});
            skLineSegment(sketch, "E74.left", {"start": v(3.7, 8.35) * mm, "end": v(3.7, 7.63) * mm});
            skLineSegment(sketch, "E74.right", {"start": v(-3.7, 8.35) * mm, "end": v(-3.7, 7.63) * mm});
            skSolve(sketch);
        }
        {
            var Q0;
            Q0 = qSketchRegion(id + "F68", true);
            extrude(context, id + "F69", {"entities" : qUnion([Q0]), "operationType" : NewBodyOperationType.REMOVE, "oppositeDirection" : true, "depth" : 1 * mm, "offsetDistance" : 25 * mm});
        }
        {
            var Q0;
            Q0=makeQuery(id+"F39.boolean.opBoolean","MERGE",FACE,{"derivedFrom":[makeQuery(id+"F17.boolean.opBoolean","MERGE",FACE,{"derivedFrom":[makeQuery(id+"F9.boolean.opBoolean","MERGE",FACE,{"derivedFrom":[makeQuery(id+"F1.opExtrude","SWEPT_FACE",FACE,{"disambiguationData":[OSD([sQuery(id+"F0.wireOp",EDGE,"E0.bottom")])]}),makeQuery(id+"F9.opExtrude","SWEPT_FACE",FACE,{"disambiguationData":[OSD([sQuery(id+"F8.wireOp",EDGE,"E11.top")])]})]}),makeQuery(id+"F17.opExtrude","SWEPT_FACE",FACE,{"disambiguationData":[OSD([sQuery(id+"F16.wireOp",EDGE,"E21.top")])]})]}),makeQuery(id+"F39.opExtrude","SWEPT_FACE",FACE,{"disambiguationData":[OSD([sQuery(id+"F38.wireOp",EDGE,"E51.bottom")])]})]});
            var sketch = newSketch(context, id + "F70", { "sketchPlane" : qUnion([Q0])});
            skLineSegment(sketch, "E75.bottom", {"start": v(12.77, 3.81) * mm, "end": v(8.53, 3.81) * mm});
            skLineSegment(sketch, "E75.top", {"start": v(12.77, -3.7) * mm, "end": v(8.53, -3.7) * mm});
            skLineSegment(sketch, "E75.left", {"start": v(12.77, 3.81) * mm, "end": v(12.77, -3.7) * mm});
            skLineSegment(sketch, "E75.right", {"start": v(8.53, 3.81) * mm, "end": v(8.53, -3.7) * mm});
            skSolve(sketch);
        }
        {
            var Q0;
            {var subQ3=sQuery(id+"F70.wireOp",EDGE,"E75.bottom");Q0=makeQuery(id+"F70.imprint","IMPRINT",FACE,{"disambiguationData":[TD([[makeQuery(id+"F70.imprint","IMPRINT",EDGE,{"derivedFrom":subQ3}),1.0]])]});}
            extrude(context, id + "F71", {"entities" : qUnion([Q0]), "operationType" : NewBodyOperationType.REMOVE, "endBound" : BoundingType.THROUGH_ALL, "oppositeDirection" : true, "depth" : 25 * mm, "offsetDistance" : 25 * mm});
        }
        {
            var Q0;
            Q0=makeQuery(id+"F15.boolean.opBoolean","COPY",FACE,{"derivedFrom":makeQuery(id+"F15.opExtrude","SWEPT_FACE",FACE,{"disambiguationData":[OSD([sQuery(id+"F14.wireOp",EDGE,"E19.top")])]})});
            var sketch = newSketch(context, id + "F72", { "sketchPlane" : qUnion([Q0])});
            skLineSegment(sketch, "E76.bottom", {"start": v(60.3, 3.69) * mm, "end": v(68.2, 3.69) * mm});
            skLineSegment(sketch, "E76.top", {"start": v(60.3, -3.83) * mm, "end": v(68.2, -3.83) * mm});
            skLineSegment(sketch, "E76.left", {"start": v(60.3, 3.69) * mm, "end": v(60.3, -3.83) * mm});
            skLineSegment(sketch, "E76.right", {"start": v(68.2, 3.69) * mm, "end": v(68.2, -3.83) * mm});
            skSolve(sketch);
        }
        {
            var Q0;
            {var subQ4=sQuery(id+"F72.wireOp",EDGE,"E76.bottom");Q0=makeQuery(id+"F72.imprint","IMPRINT",FACE,{"disambiguationData":[TD([[makeQuery(id+"F72.imprint","IMPRINT",EDGE,{"derivedFrom":subQ4}),-1.0]])]});}
            extrude(context, id + "F73", {"entities" : qUnion([Q0]), "operationType" : NewBodyOperationType.REMOVE, "endBound" : BoundingType.THROUGH_ALL, "oppositeDirection" : true, "depth" : 25 * mm, "offsetDistance" : 25 * mm});
        }
        {
            var Q0;
            Q0=makeQuery(id+"F1.opExtrude","SWEPT_FACE",FACE,{"disambiguationData":[OSD([sQuery(id+"F0.wireOp",EDGE,"E0.right")])]});
            var sketch = newSketch(context, id + "F74", { "sketchPlane" : qUnion([Q0])});
            skLineSegment(sketch, "E77.bottom", {"start": v(-5.75, 1.58) * mm, "end": v(5.75, 1.58) * mm});
            skLineSegment(sketch, "E77.top", {"start": v(-5.75, 3.18) * mm, "end": v(5.75, 3.18) * mm});
            skLineSegment(sketch, "E77.left", {"start": v(-5.75, 1.58) * mm, "end": v(-5.75, 3.18) * mm});
            skLineSegment(sketch, "E77.right", {"start": v(5.75, 1.58) * mm, "end": v(5.75, 3.18) * mm});
            skSolve(sketch);
        }
        {
            var Q0;
            Q0=makeQuery(id+"F74.imprint","IMPRINT",FACE,{"disambiguationData":[TD([[makeQuery(id+"F74.imprint","IMPRINT",EDGE,{"derivedFrom":sQuery(id+"F74.wireOp",EDGE,"E77.bottom")}),-1.0]])]});
            extrude(context, id + "F75", {"entities" : qUnion([Q0]), "operationType" : NewBodyOperationType.REMOVE, "oppositeDirection" : true, "depth" : 20 * mm, "offsetDistance" : 25 * mm});
        }
        {
            var Q0;
            Q0=makeQuery(id+"F39.opExtrude","SWEPT_FACE",FACE,{"disambiguationData":[OSD([sQuery(id+"F38.wireOp",EDGE,"E51.top")])]});
            var sketch = newSketch(context, id + "F76", { "sketchPlane" : qUnion([Q0])});
            skLineSegment(sketch, "E78.bottom", {"start": v(24.6, 3.69) * mm, "end": v(8.54, 3.69) * mm});
            skLineSegment(sketch, "E78.top", {"start": v(24.6, 4.69) * mm, "end": v(8.54, 4.69) * mm});
            skLineSegment(sketch, "E78.left", {"start": v(24.6, 3.69) * mm, "end": v(24.6, 4.69) * mm});
            skLineSegment(sketch, "E78.right", {"start": v(8.54, 3.69) * mm, "end": v(8.54, 4.69) * mm});
            skLineSegment(sketch, "E79.bottom", {"start": v(8.53, -3.81) * mm, "end": v(24.6, -3.81) * mm});
            skLineSegment(sketch, "E79.top", {"start": v(8.53, -4.81) * mm, "end": v(24.6, -4.81) * mm});
            skLineSegment(sketch, "E79.left", {"start": v(8.53, -3.81) * mm, "end": v(8.53, -4.81) * mm});
            skLineSegment(sketch, "E79.right", {"start": v(24.6, -3.81) * mm, "end": v(24.6, -4.81) * mm});
            skSolve(sketch);
        }
        {
            var Q0;
            Q0 = qSketchRegion(id + "F76", true);
            extrude(context, id + "F77", {"entities" : qUnion([Q0]), "operationType" : NewBodyOperationType.REMOVE, "endBound" : BoundingType.THROUGH_ALL, "oppositeDirection" : true, "depth" : 25 * mm, "offsetDistance" : 25 * mm});
        }
    });
